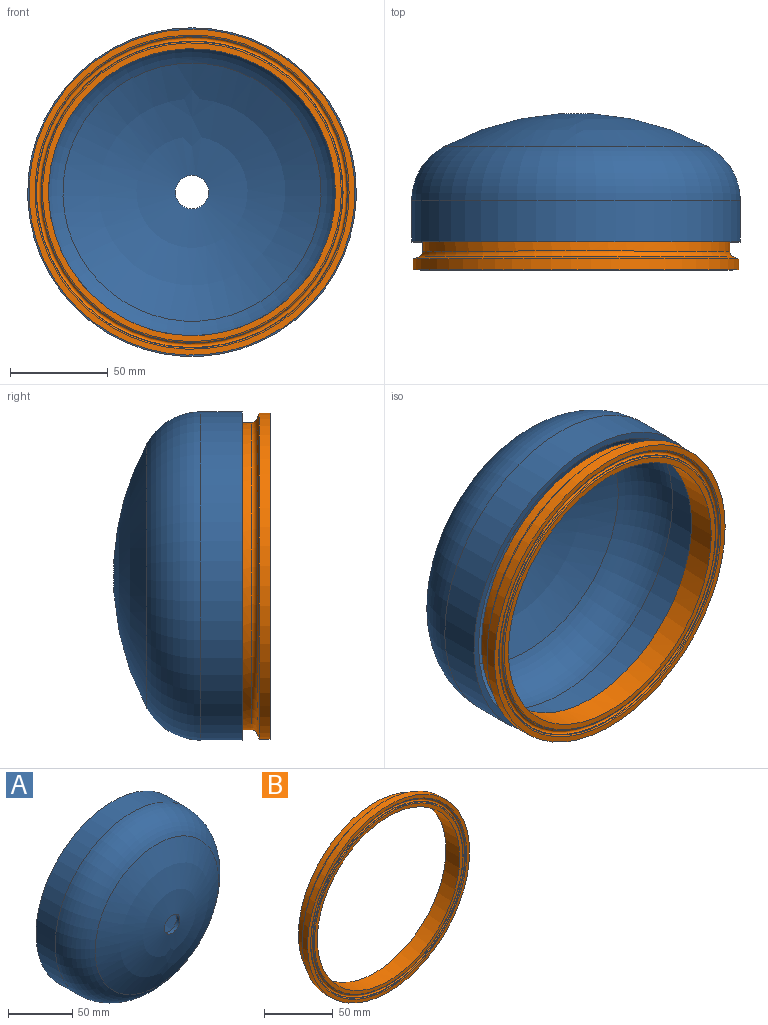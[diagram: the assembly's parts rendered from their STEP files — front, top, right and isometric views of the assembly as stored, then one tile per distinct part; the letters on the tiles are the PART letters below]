
ASSEMBLY  parts=2 mates=1
PART A: 8 faces, bbox 182.1x65.6x182.1 mm
  f0: sphere r=142.06mm, area 15096.4mm2, adj f3,f7
  f1: sphere r=138.66mm, area 14370.7mm2, adj f5,f7
  f2: plane 168.28x168.28mm, normal (0,1,0), area 1762.9mm2, adj f4,f6
  f3: torus R=52.74mm, axis (0,-1,0), area 16618.3mm2, adj f0,f4
  f4: cylinder r=84.14mm len=168.28mm, axis (0,-1,0), area 11158.5mm2, adj f2,f3
  f5: torus R=52.74mm, axis (0,-1,0), area 14290.4mm2, adj f1,f6
  f6: cylinder r=80.73mm len=161.47mm, axis (0,-1,0), area 10707.1mm2, adj f2,f5
  f7: cylinder r=8.57mm len=17.15mm, axis (0,1,0), area 183.7mm2, adj f0,f1
PART B: 13 faces, bbox 177.1x14.3x177.1 mm
  f0: cylinder r=83.44mm len=166.88mm, axis (0,-1,0), area 2929.6mm2, adj f1,f10
  f1: cone r=80.73mm half-angle=70deg, axis (0,-1,0), area 1488.2mm2, adj f0,f2
  f2: torus R=81.81mm, axis (0,-1,0), area 1934.5mm2, adj f1,f3
  f3: cylinder r=78.64mm len=157.28mm, axis (0,-1,0), area 2336.6mm2, adj f2,f12
  f4: cylinder r=73.43mm len=146.86mm, axis (0,-1,0), area 6592mm2, adj f11,f12
  f5: torus R=76.44mm, axis (0,-1,0), area 444.6mm2, adj f6,f11
  f6: cone r=77.34mm half-angle=23deg, axis (0,1,0), area 207.3mm2, adj f5,f7
  f7: torus R=78.44mm, axis (0,-1,0), area 1376mm2, adj f6,f8
  f8: cone r=79.7mm half-angle=23deg, axis (0,-1,0), area 213.6mm2, adj f7,f9
  f9: torus R=80.43mm, axis (0,-1,0), area 462.9mm2, adj f8,f10
  f10: plane 166.88x166.88mm, normal (0,-1,0), area 1551.2mm2, adj f0,f9
  f11: plane 152.89x152.89mm, normal (0,-1,0), area 1418.8mm2, adj f4,f5
  f12: plane 157.28x157.28mm, normal (0,1,0), area 2487.6mm2, adj f3,f4
PLACE A rot(axis=(-1,0,0),180deg) t=(0,14.29,0)mm
PLACE B at identity
MATE fastened A.f3 <-> B.f0  axis (0,-1,0) through (0,14.29,0)mm
